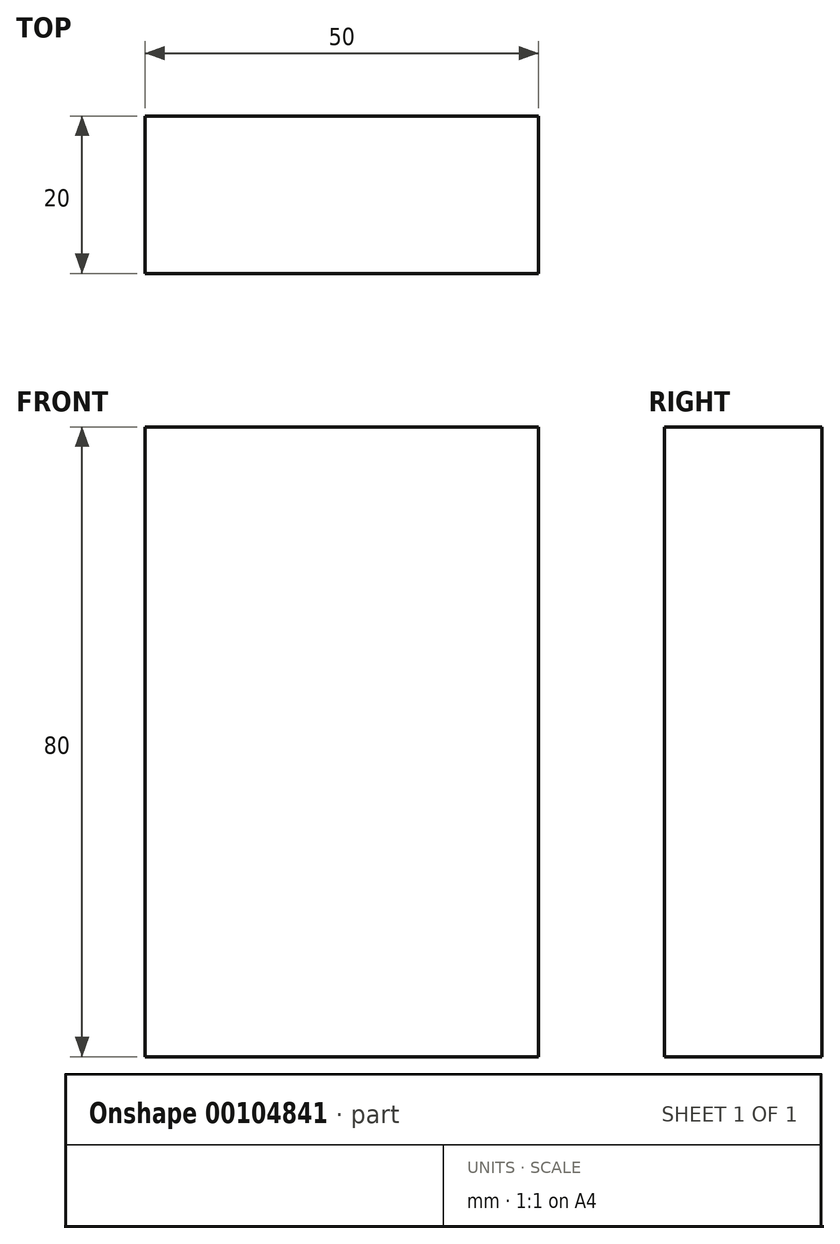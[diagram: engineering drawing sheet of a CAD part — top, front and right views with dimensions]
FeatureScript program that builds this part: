
annotation { "Feature Type Name" : "Feature", "Feature Type Description" : "" }
export const myFeature = defineFeature(function(context is Context, id is Id, definition is map)
    precondition{}
    {
        {
            var Q0;
            Q0=qCreatedBy(makeId("Front.planeOp"),FACE);
            var sketch = newSketch(context, id + "F0", { "sketchPlane" : qUnion([Q0])});
            skLineSegment(sketch, "E0.bottom", {"start": v(-1.43, 78.96) * mm, "end": v(48.57, 78.96) * mm});
            skLineSegment(sketch, "E0.top", {"start": v(-1.43, -1.04) * mm, "end": v(48.57, -1.04) * mm});
            skLineSegment(sketch, "E0.left", {"start": v(-1.43, 78.96) * mm, "end": v(-1.43, -1.04) * mm});
            skLineSegment(sketch, "E0.right", {"start": v(48.57, 78.96) * mm, "end": v(48.57, -1.04) * mm});
            skSolve(sketch);
        }
        {
            var Q0;
            Q0 = qSketchRegion(id + "F0", true);
            extrude(context, id + "F1", {"entities" : qUnion([Q0]), "depth" : 20 * mm});
        }
    });
